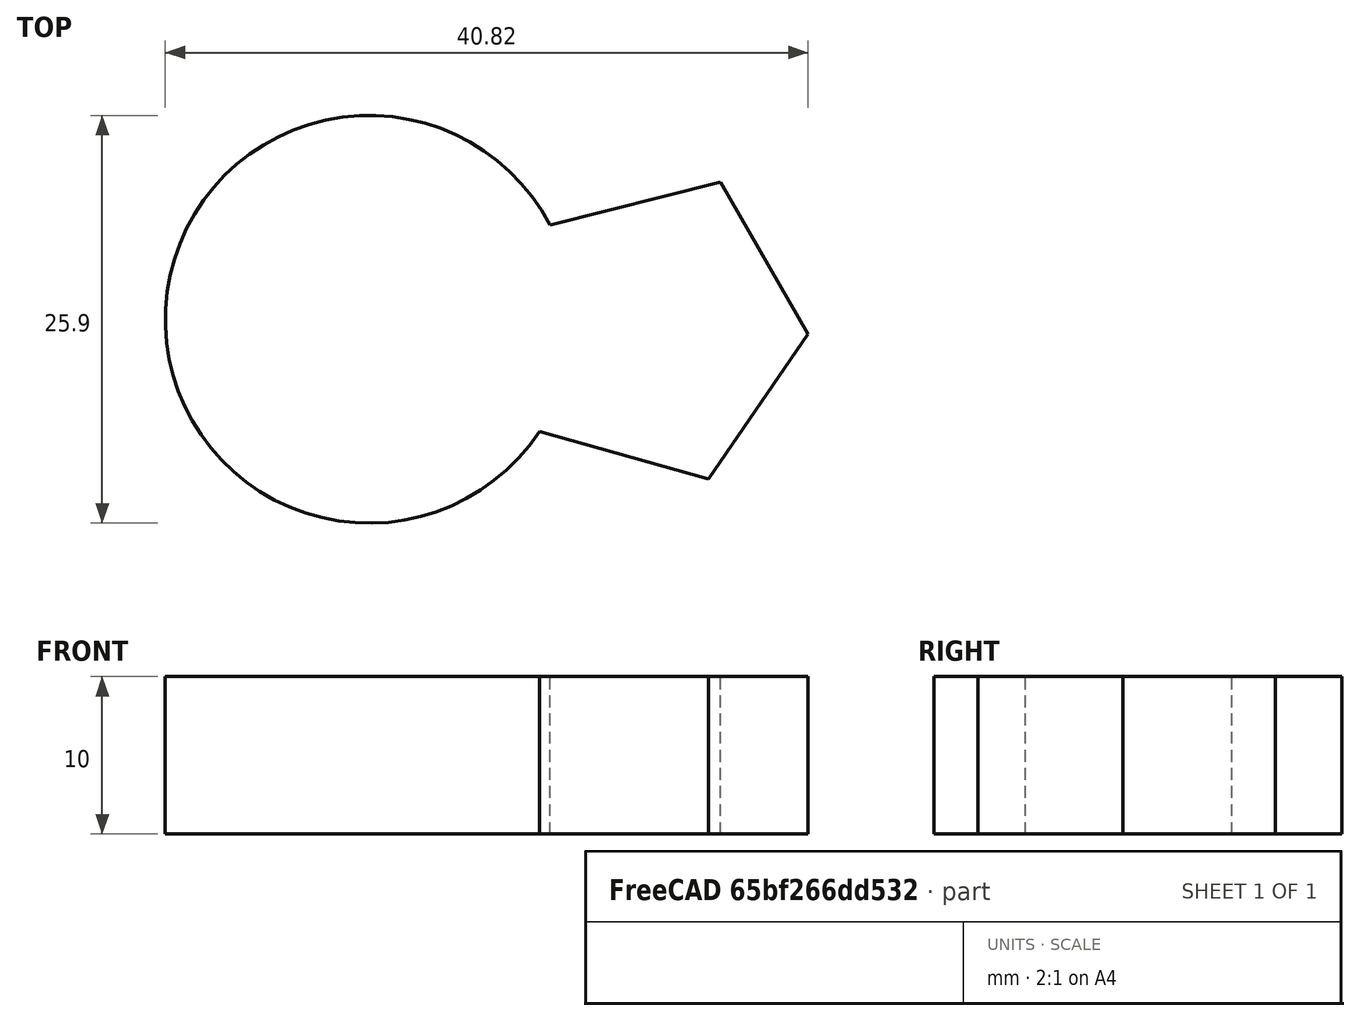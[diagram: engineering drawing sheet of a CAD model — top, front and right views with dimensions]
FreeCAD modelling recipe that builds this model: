
FCSTD DOCUMENT  (FreeCAD 0.18R4 (GitTag))
Label: FreeCADTutorial1
License: All rights reserved
LicenseURL: http://en.wikipedia.org/wiki/All_rights_reserved
objects: Sketcher::SketchObject×1, PartDesign::Pad×1, PartDesign::Body×1
note: 4 computed .brp shape members not serialized (recipe doc carries the construction recipe); baked Part::Feature solids carry a one-line shape summary decoded from their .brp

FEATURE [Sketcher::SketchObject] Sketch
  MapMode = 5
  Support = -> [XY_Plane]
  sketch-geometry (7):
    g0: ArcOfCircle CenterX=19.3083 CenterY=22.9403 CenterZ=0 NormalX=0 NormalY=0 NormalZ=1 AngleXU=0 Radius=12.9488 StartAngle=0.480099 EndAngle=5.70057
    g1: LineSegment StartX=47.1805 StartY=21.9911 StartZ=0 EndX=41.6141 EndY=31.6686 EndZ=0
    g2: LineSegment StartX=41.6141 StartY=31.6686 StartZ=0 EndX=30.7932 EndY=28.9209 EndZ=0
    g3: LineSegment StartX=30.1209 StartY=15.8157 StartZ=0 EndX=40.8657 EndY=12.7843 EndZ=0
    g4: LineSegment StartX=40.8657 StartY=12.7843 StartZ=0 EndX=47.1805 EndY=21.9911 EndZ=0
    g5: Circle [constr] CenterX=36.7064 CenterY=22.4061 CenterZ=0 NormalX=0 NormalY=0 NormalZ=1 AngleXU=0 Radius=10.4823
    g6: LineSegment [constr] StartX=55.0187 StartY=30.993 StartZ=0 EndX=47.3289 EndY=10.2044 EndZ=0
  constraints (11):
    c: Coincident(g1,g2)
    c: Coincident(g3,g4)
    c: Coincident(g4,g1)
    c: Equal(g1,g2)
    c: Equal(g1,g3)
    c: Equal(g1,g4)
    c: PointOnObject(g1,g5)
    c: PointOnObject(g3,g5)
    c: PointOnObject(g4,g5)
    c: Coincident(g0,g2)
    c: Coincident(g0,g3)
FEATURE [PartDesign::Pad] Pad
  Length = 10
  Length2 = 100
  Profile = -> Sketch
  Type = 0
FEATURE [PartDesign::Body] Body
  Group = -> [Sketch,Pad]
  Origin = -> Origin
  Tip = -> Pad
